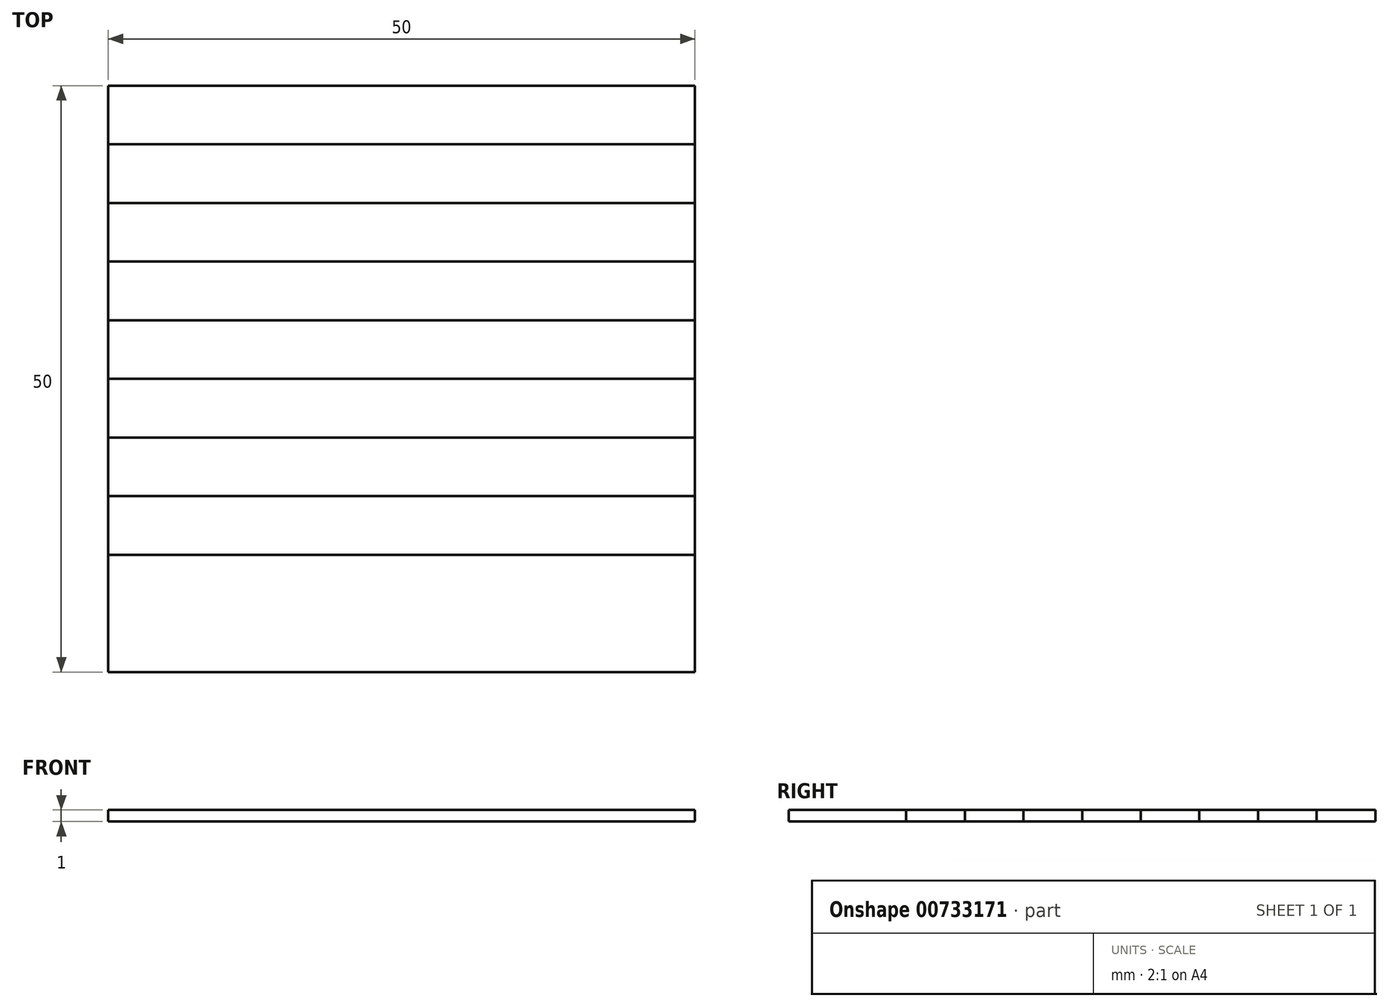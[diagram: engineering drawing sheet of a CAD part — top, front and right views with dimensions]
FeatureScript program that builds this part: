
annotation { "Feature Type Name" : "Feature", "Feature Type Description" : "" }
export const myFeature = defineFeature(function(context is Context, id is Id, definition is map)
    precondition{}
    {
        {
            var Q0;
            Q0=qCreatedBy(makeId("Top.planeOp"),FACE);
            var sketch = newSketch(context, id + "F0", { "sketchPlane" : qUnion([Q0])});
            skLineSegment(sketch, "E0.bottom", {"start": v(0, 50) * mm, "end": v(50, 50) * mm});
            skLineSegment(sketch, "E0.top", {"start": v(0, -50) * mm, "end": v(50, -50) * mm});
            skLineSegment(sketch, "E0.left", {"start": v(0, 50) * mm, "end": v(0, -50) * mm});
            skLineSegment(sketch, "E0.right", {"start": v(50, 50) * mm, "end": v(50, -50) * mm});
            skLineSegment(sketch, "E1", {"start": v(0, 10) * mm, "end": v(50, 10) * mm});
            skLineSegment(sketch, "E2", {"start": v(0, -10) * mm, "end": v(50, -10) * mm});
            skLineSegment(sketch, "E3", {"start": v(0, 15) * mm, "end": v(50, 15) * mm});
            skLineSegment(sketch, "E4", {"start": v(0, 20) * mm, "end": v(50, 20) * mm});
            skLineSegment(sketch, "E5", {"start": v(0, 25) * mm, "end": v(50, 25) * mm});
            skLineSegment(sketch, "E6", {"start": v(0, 30) * mm, "end": v(50, 30) * mm});
            skLineSegment(sketch, "E7", {"start": v(0, 35) * mm, "end": v(50, 35) * mm});
            skLineSegment(sketch, "E8", {"start": v(0, 40) * mm, "end": v(50, 40) * mm});
            skLineSegment(sketch, "E9", {"start": v(0, 45) * mm, "end": v(50, 45) * mm});
            skLineSegment(sketch, "E10", {"start": v(0, 0) * mm, "end": v(50, 0) * mm});
            skSolve(sketch);
        }
        {
            var Q0;
            {var subQ0=sQuery(id+"F0.wireOp",EDGE,"E1");Q0=makeQuery(id+"F0.imprint","IMPRINT",FACE,{"disambiguationData":[TD([[makeQuery(id+"F0.imprint","IMPRINT",EDGE,{"derivedFrom":subQ0}),-1.0]])]});}
            var Q1;
            {var subQ0=sQuery(id+"F0.wireOp",EDGE,"E3");Q1=makeQuery(id+"F0.imprint","IMPRINT",FACE,{"disambiguationData":[TD([[makeQuery(id+"F0.imprint","IMPRINT",EDGE,{"derivedFrom":subQ0}),1.0]])]});}
            var Q2;
            {var subQ0=sQuery(id+"F0.wireOp",EDGE,"E5");Q2=makeQuery(id+"F0.imprint","IMPRINT",FACE,{"disambiguationData":[TD([[makeQuery(id+"F0.imprint","IMPRINT",EDGE,{"derivedFrom":subQ0}),1.0]])]});}
            var Q3;
            {var subQ0=sQuery(id+"F0.wireOp",EDGE,"E7");Q3=makeQuery(id+"F0.imprint","IMPRINT",FACE,{"disambiguationData":[TD([[makeQuery(id+"F0.imprint","IMPRINT",EDGE,{"derivedFrom":subQ0}),1.0]])]});}
            var Q4;
            {var subQ0=sQuery(id+"F0.wireOp",EDGE,"E0.bottom");Q4=makeQuery(id+"F0.imprint","IMPRINT",FACE,{"disambiguationData":[TD([[makeQuery(id+"F0.imprint","IMPRINT",EDGE,{"derivedFrom":subQ0}),-1.0]])]});}
            extrude(context, id + "F1", {"entities" : qUnion([Q0, Q1, Q2, Q3, Q4]), "endBound" : BoundingType.SYMMETRIC, "depth" : 1 * mm, "offsetDistance" : 25 * mm});
        }
        {
            var Q0;
            {var subQ0=sQuery(id+"F0.wireOp",EDGE,"E8");Q0=makeQuery(id+"F0.imprint","IMPRINT",FACE,{"disambiguationData":[TD([[makeQuery(id+"F0.imprint","IMPRINT",EDGE,{"derivedFrom":subQ0}),1.0]])]});}
            var Q1;
            {var subQ0=sQuery(id+"F0.wireOp",EDGE,"E6");Q1=makeQuery(id+"F0.imprint","IMPRINT",FACE,{"disambiguationData":[TD([[makeQuery(id+"F0.imprint","IMPRINT",EDGE,{"derivedFrom":subQ0}),1.0]])]});}
            var Q2;
            {var subQ0=sQuery(id+"F0.wireOp",EDGE,"E4");Q2=makeQuery(id+"F0.imprint","IMPRINT",FACE,{"disambiguationData":[TD([[makeQuery(id+"F0.imprint","IMPRINT",EDGE,{"derivedFrom":subQ0}),1.0]])]});}
            var Q3;
            {var subQ0=sQuery(id+"F0.wireOp",EDGE,"E1");Q3=makeQuery(id+"F0.imprint","IMPRINT",FACE,{"disambiguationData":[TD([[makeQuery(id+"F0.imprint","IMPRINT",EDGE,{"derivedFrom":subQ0}),1.0]])]});}
            extrude(context, id + "F2", {"entities" : qUnion([Q0, Q1, Q2, Q3]), "endBound" : BoundingType.SYMMETRIC, "depth" : 1 * mm, "offsetDistance" : 25 * mm});
        }
    });
